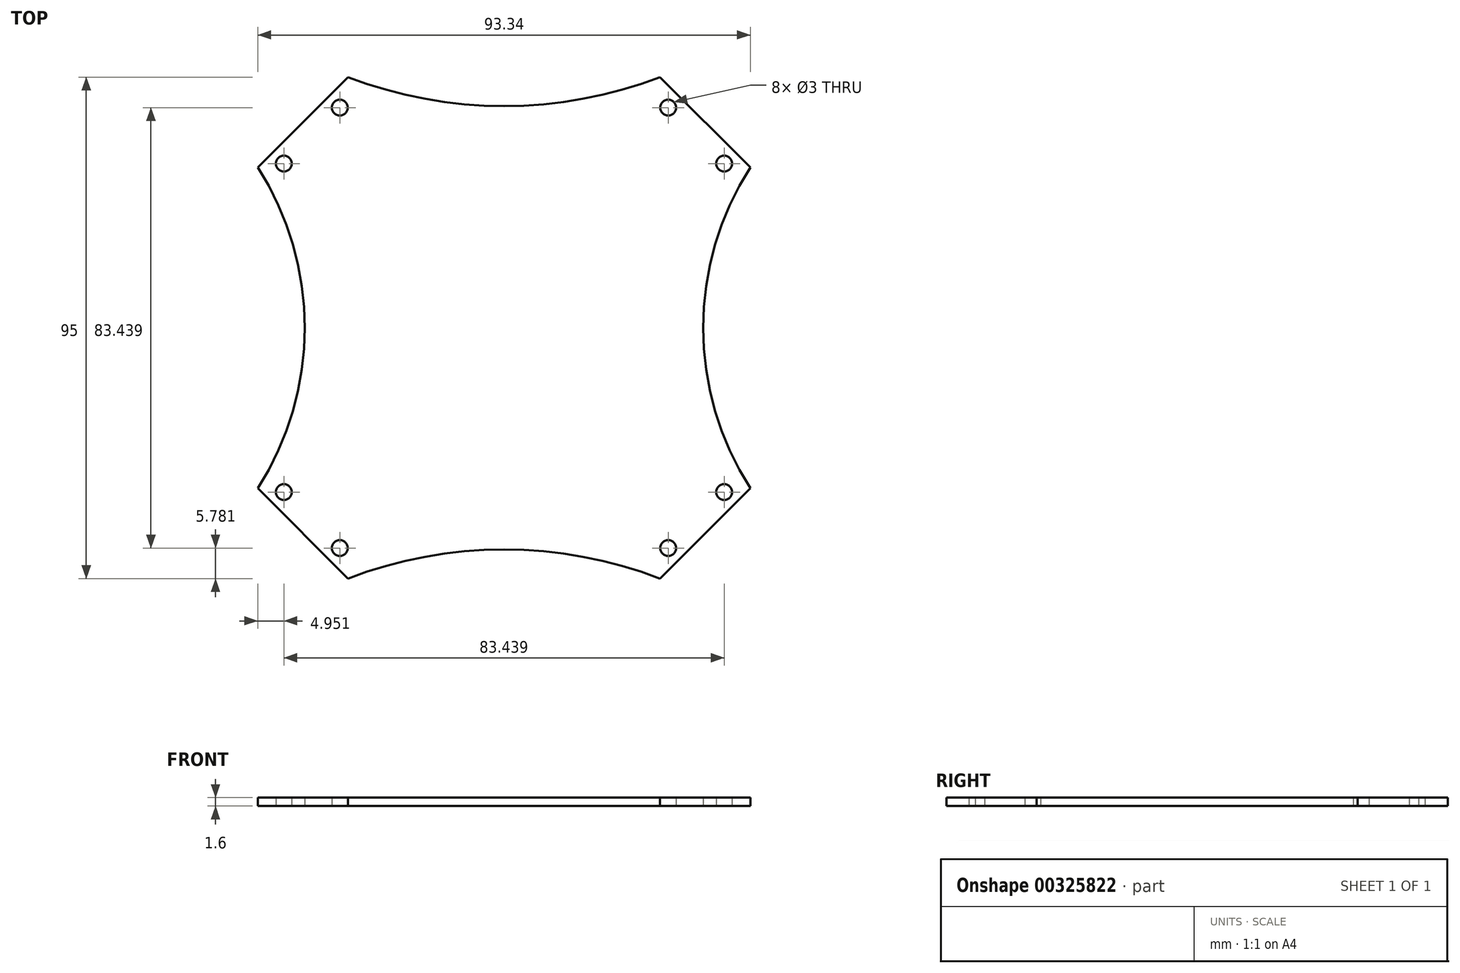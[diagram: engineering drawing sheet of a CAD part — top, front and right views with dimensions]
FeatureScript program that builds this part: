
annotation { "Feature Type Name" : "Feature", "Feature Type Description" : "" }
export const myFeature = defineFeature(function(context is Context, id is Id, definition is map)
    precondition{}
    {
        {
            var Q0;
            Q0=qCreatedBy(makeId("Top.planeOp"),FACE);
            var sketch = newSketch(context, id + "F0", { "sketchPlane" : qUnion([Q0])});
            skLineSegment(sketch, "E0", {"start": v(0, 0) * mm, "end": v(-49.78, 0) * mm, "construction": true});
            skLineSegment(sketch, "E1", {"start": v(0, 0) * mm, "end": v(0, 52.64) * mm, "construction": true});
            skLineSegment(sketch, "E2", {"start": v(0, 0) * mm, "end": v(-51.06, 51.06) * mm, "construction": true});
            skLineSegment(sketch, "E3", {"start": v(-45.07, 27.76) * mm, "end": v(-28.64, 44.2) * mm, "construction": true});
            skCircle(sketch, "E4", {"center": v(-41.72, 31.11) * mm, "radius": 1.5 * mm});
            skCircle(sketch, "E5", {"center": v(-31.11, 41.72) * mm, "radius": 1.5 * mm});
            skLineSegment(sketch, "E6", {"start": v(-46.67, 30.4) * mm, "end": v(-29.57, 47.5) * mm});
            skLineSegment(sketch, "E7.MirrorCS", {"start": v(46.67, 30.4) * mm, "end": v(29.57, 47.5) * mm});
            skCircle(sketch, "E8.MirrorC", {"center": v(31.11, 41.72) * mm, "radius": 1.5 * mm});
            skCircle(sketch, "E9.MirrorC", {"center": v(41.72, 31.11) * mm, "radius": 1.5 * mm});
            skLineSegment(sketch, "E10.MirrorCS", {"start": v(-46.67, -30.4) * mm, "end": v(-29.57, -47.5) * mm});
            skLineSegment(sketch, "E11.MirrorCS", {"start": v(46.67, -30.4) * mm, "end": v(29.57, -47.5) * mm});
            skCircle(sketch, "E12.MirrorC", {"center": v(41.72, -31.11) * mm, "radius": 1.5 * mm});
            skCircle(sketch, "E13.MirrorC", {"center": v(31.11, -41.72) * mm, "radius": 1.5 * mm});
            skCircle(sketch, "E14.MirrorC", {"center": v(-31.11, -41.72) * mm, "radius": 1.5 * mm});
            skCircle(sketch, "E15.MirrorC", {"center": v(-41.72, -31.11) * mm, "radius": 1.5 * mm});
            skArc(sketch, "E16", {"start": v(-46.67, -30.4) * mm, "mid": v(-37.75, 0) * mm, "end": v(-46.67, 30.4) * mm});
            skArc(sketch, "E17.MirrorCS", {"start": v(46.67, -30.4) * mm, "mid": v(37.75, 0) * mm, "end": v(46.67, 30.4) * mm});
            skPoint(sketch, "E18.orphan", {"position": v(-27.13, 42) * mm});
            skArc(sketch, "E19", {"start": v(29.57, -47.5) * mm, "mid": v(0, -42) * mm, "end": v(-29.57, -47.5) * mm});
            skArc(sketch, "E20.MirrorCS", {"start": v(29.57, 47.5) * mm, "mid": v(0, 42) * mm, "end": v(-29.57, 47.5) * mm});
            skPoint(sketch, "E21", {"position": v(-36.42, 36.42) * mm});
            skSolve(sketch);
        }
        {
            var Q0;
            Q0=makeQuery(id+"F0.imprint","IMPRINT",FACE,{"disambiguationData":[TD([[makeQuery(id+"F0.imprint","IMPRINT",EDGE,{"derivedFrom":sQuery(id+"F0.wireOp",EDGE,"E4")}),-1.0]])]});
            extrude(context, id + "F1", {"entities" : qUnion([Q0]), "depth" : 1.6 * mm});
        }
    });
